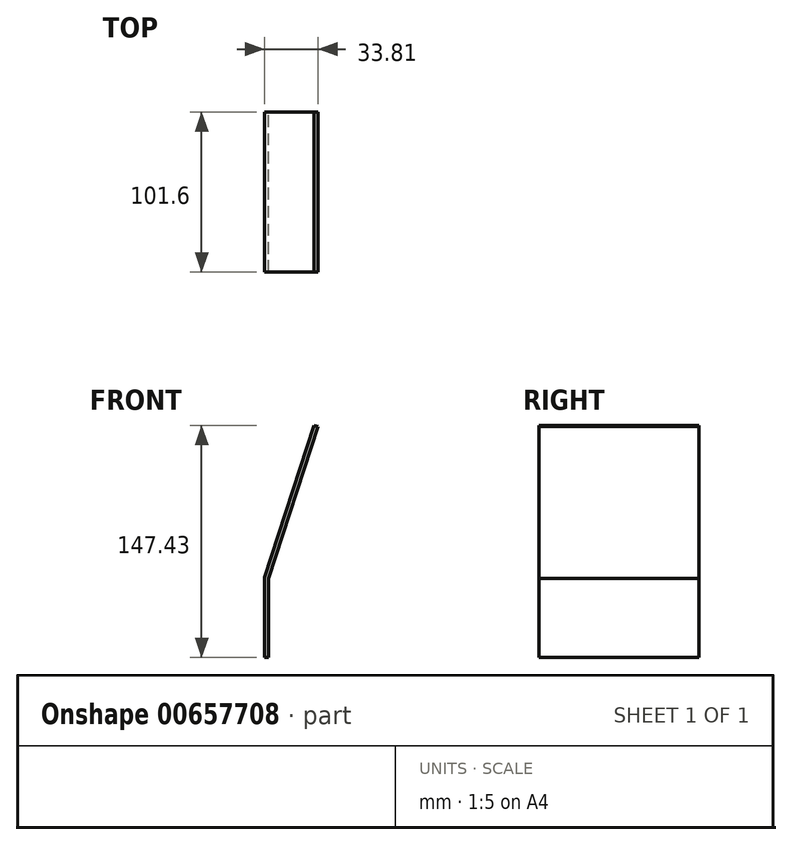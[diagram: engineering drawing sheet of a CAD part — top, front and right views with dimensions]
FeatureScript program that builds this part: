
annotation { "Feature Type Name" : "Feature", "Feature Type Description" : "" }
export const myFeature = defineFeature(function(context is Context, id is Id, definition is map)
    precondition{}
    {
        {
            var Q0;
            Q0=qCreatedBy(makeId("Front.planeOp"),FACE);
            var sketch = newSketch(context, id + "F0", { "sketchPlane" : qUnion([Q0])});
            skLineSegment(sketch, "E0", {"start": v(0, 0) * mm, "end": v(0, -50.8) * mm});
            skLineSegment(sketch, "E1", {"start": v(0, -50.8) * mm, "end": v(2.54, -50.8) * mm});
            skLineSegment(sketch, "E2", {"start": v(0, 0) * mm, "end": v(31.4, 96.63) * mm});
            skLineSegment(sketch, "E3", {"start": v(0, 0) * mm, "end": v(25.09, -3.97) * mm});
            skLineSegment(sketch, "E4", {"start": v(2.54, -50.8) * mm, "end": v(2.54, -0.4) * mm});
            skLineSegment(sketch, "E5", {"start": v(31.4, 96.63) * mm, "end": v(33.81, 95.84) * mm});
            skLineSegment(sketch, "E6", {"start": v(33.81, 95.84) * mm, "end": v(2.54, -0.4) * mm});
            skLineSegment(sketch, "E7.bottom", {"start": v(0, -50.8) * mm, "end": v(34.93, -50.8) * mm});
            skLineSegment(sketch, "E7.top", {"start": v(0, 203.2) * mm, "end": v(34.92, 203.2) * mm});
            skLineSegment(sketch, "E7.left", {"start": v(0, -50.8) * mm, "end": v(0, 203.2) * mm});
            skLineSegment(sketch, "E7.right", {"start": v(34.93, -50.8) * mm, "end": v(34.92, 203.2) * mm});
            skSolve(sketch);
        }
        {
            var Q0;
            {var subQ0=sQuery(id+"F0.wireOp",EDGE,"E2");Q0=makeQuery(id+"F0.imprint","IMPRINT",FACE,{"disambiguationData":[TD([[makeQuery(id+"F0.imprint","IMPRINT",EDGE,{"derivedFrom":subQ0}),-1.0]])]});}
            var Q1;
            {var subQ0=sQuery(id+"F0.wireOp",EDGE,"E0");Q1=makeQuery(id+"F0.imprint","IMPRINT",FACE,{"disambiguationData":[TD([[makeQuery(id+"F0.imprint","IMPRINT",EDGE,{"derivedFrom":subQ0}),1.0]])]});}
            var Q2;
            {var subQ3=sQuery(id+"F0.wireOp",EDGE,"E4");Q2=makeQuery(id+"F0.imprint","IMPRINT",FACE,{"disambiguationData":[TD([[makeQuery(id+"F0.imprint","IMPRINT",EDGE,{"derivedFrom":subQ3}),1.0]])]});}
            extrude(context, id + "F1", {"entities" : qUnion([Q0, Q1, Q2]), "depth" : 101.6 * mm, "offsetDistance" : 25.4 * mm});
        }
    });
